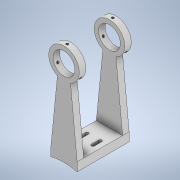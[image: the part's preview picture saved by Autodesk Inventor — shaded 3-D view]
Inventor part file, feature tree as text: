
AUTODESK INVENTOR PART (.ipt)
format: ipt  version: 2020.3 (Build 243373000, 373)  size: 3,882,496 bytes
history: native  units: in
note: dims shown in document units (in); Inventor stores cm internally (conversion verified against a paired STEP export)
features: sketch x17, thread x6, revolve x6, helix x6, extrude x5, plane x2, pattern_circular x1, mirror x1
ambient origin geometry x8: Origin, YZ Plane, XZ Plane, XY Plane, X Axis, Y Axis, Z Axis, Center Point
bodies: Solid1 (feature_tree), Solid2 (feature_tree), Solid3 (feature_tree), Solid4 (feature_tree), Solid5 (feature_tree), Solid6 (feature_tree), Solid7 (feature_tree)
feature tree (44):
  extrude  "Extrusion1"  Depth=0.75in
  extrude  "Extrusion2"  Depth=2.979in TaperAngle=0.0deg
  plane  "Work Plane1"
  extrude  "Extrusion3"  Depth=0.175in
  extrude  "Extrusion4"  Depth=0.75in
  plane  "Work Plane2"
  extrude  "Extrusion5"  Depth=0.4in
  pattern_circular  "Circular Pattern1"  Count=3 Angle=360.0deg
  mirror  "Mirror1"
  thread  "Thread1"  [1 undecoded]
  thread  "Thread2"  [1 undecoded]
  thread  "Thread3"  [1 undecoded]
  thread  "Thread4"  [1 undecoded]
  thread  "Thread5"  [1 undecoded]
  thread  "Thread6"  [1 undecoded]
  revolve  "Revolution1"  Angle=60.0deg
  helix  "Coil1"  [1 undecoded]
  revolve  "Revolution2"  [1 undecoded]
  helix  "Coil2"  [1 undecoded]
  revolve  "Revolution3"  [1 undecoded]
  helix  "Coil3"  [1 undecoded]
  revolve  "Revolution4"  [1 undecoded]
  helix  "Coil4"  [1 undecoded]
  revolve  "Revolution5"  [1 undecoded]
  helix  "Coil5"  [1 undecoded]
  revolve  "Revolution6"  [1 undecoded]
  helix  "Coil6"  [1 undecoded]
  sketch  "Sketch1"  dims[d0=6.0in d1=0.75in]
  sketch  "Sketch2"  dims[d2=0.5in d3=2.979in d4=0.0in]
  sketch  "Sketch4"  dims[d5=0.375in d6=0.175in]
  sketch  "Sketch5"  dims[d7=0.6in d8=0.75in]
  sketch  "Sketch6"  dims[d9=0.0in d10=0.0in d11=0.4in]
  sketch  "Sketch8"  dims[d12=0.75in]
  sketch  "Sketch9"  dims[d13=0.3in d14=0.0in]
  sketch  "Sketch10"  dims[d15=1.25in]
  sketch  "Sketch11"  dims[d16=0.25in]
  sketch  "Sketch12"  dims[d17=5.0in]
  sketch  "Sketch13"  dims[d18=0.375in]
  sketch  "Sketch14"  dims[d19=0.375in d20=0.0in]
  sketch  "Sketch15"  dims[d21=0.1875in]
  sketch  "Sketch16"  dims[d22=0.136in]
  sketch  "Sketch17"  dims[d23=0.0in d24=0.0in d25=1.1811in d26=360.0deg d30=0.254in d31=0.0in d32=0.254in d33=0.0in d34=0.254in d35=0.0in d36=0.254in d37=0.0in d38=0.254in d39=0.0in d40=0.254in d41=0.0in]
  sketch  "Sketch18"  dims[d42=0.0068in d43=0.0039in d44=0.002in d45=0.0034in d46=0.0312in d48=60.0deg d51=0.0039in]
  sketch  "Sketch19"  dims[d53=60.0deg d54=0.0in d55=0.0313in d56=0.3162in d57=0.3937in d58=0.0in d59=0.0in d60=0.0in d61=0.0in d62=0.0in d63=0.0068in d64=0.0039in d65=0.002in d66=0.0034in d67=0.0312in d69=60.0deg d72=0.0039in d74=60.0deg d75=0.0in d76=0.0313in d77=0.3162in d78=0.3937in d79=0.0in d80=0.0in d81=0.0in d82=0.0in d83=0.0in d84=0.0068in d85=0.0039in d86=0.002in d87=0.0034in d88=0.0312in d90=60.0deg d93=0.0039in d95=60.0deg d96=0.0in d97=0.0313in d98=0.3162in d99=0.3937in d100=0.0in d101=0.0in d102=0.0in d103=0.0in d104=0.0in d105=0.0068in d106=0.0039in d107=0.002in d108=0.0034in d109=0.0312in d111=60.0deg d114=0.0039in d116=60.0deg d117=0.0in d118=0.0313in d119=0.3162in d120=0.3937in d121=0.0in d122=0.0in d123=0.0in d124=0.0in d125=0.0in d126=0.0068in d127=0.0039in d128=0.002in d129=0.0034in d130=0.0312in d132=60.0deg d135=0.0039in d137=60.0deg d138=0.0in d139=0.0313in d140=0.3162in d141=0.3937in d142=0.0in d143=0.0in d144=0.0in d145=0.0in d146=0.0in d147=0.0068in d148=0.0039in d149=0.002in d150=0.0034in d151=0.0312in d153=60.0deg d156=0.0039in d158=60.0deg d159=0.0in d160=0.0313in d161=0.3162in d162=0.3937in d163=0.0in d164=0.0in d165=0.0in d166=0.0in d167=0.0in]
note: 17 required parameter values undecoded (feature->parameter linkage not recoverable at this tier; creation-order binding heuristic only, values carry confidence <= 0.55)